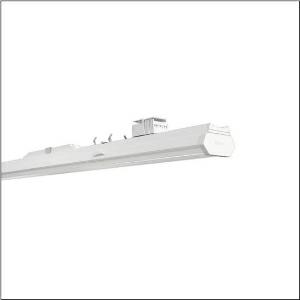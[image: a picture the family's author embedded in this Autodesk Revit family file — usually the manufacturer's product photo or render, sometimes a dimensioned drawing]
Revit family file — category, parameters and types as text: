
# Revit family: licross_21_protected_mo_52td117n485g
name_source: partatom
category: Lighting Fixtures
units: mm (PartAtom-declared; Revit-internal decimal feet)

## family parameters
Cut with Voids When Loaded = No
Host = Face
Light Source = No
Part Type = Normal
Room Calculation Point = No
Round Connector Dimension = Use Diameter
Shared = No

## types (1)
- Licross 21 Protected MO (1 x LED, 8570 lm, 47.9 W, 4000K)
    Apparent Load = 48 VA
    CIE Flux Codes = 83 94 98 100 100
    Color Rendering = 80
    Color Temperature = 4000K
    Default Elevation = 1800 mm
    Description = Licross 21 Protected MO, luminaire insert, of sheet steel, galvanised, coil coated, white, length: 1.500mm, width: 66mm, height: 67mm, LED rated luminous flux: 8.570lm, light colour: 840, SDCM (Standard Deviation of Colour Matching)MacAdam ≤ 3 SDCM (initial), control gear: ON/OFF, with plug, 3-pole, with phase selection, mains connection: 220..240V, AC, 50/60Hz, rated input power: 48W, internal wiring halogen-free, primary light control with lens, of plastic, primary optical cover: cover, of PMMA, light emission: direct distribution, primary light characteristic: symmetric, protection rating (complete): IP54, insulation class (complete): insulation class I (protective earthing), certification: CE, ENEC, VDE, UKCA, protection symbol: D if used in an environment with non-conductive dust loads with corresponding accessories, impact resistance: IK06, permissible ambient temperature for indoor applications: -35..+45°C, corresponds to IFS (International Featured Standards) requirements for safety and quality in the food industry, reducing of maximum allowable ambient temperature of 5°C with ceiling mounting, LABS conformity tested according to VDMA 24364:2018-05, The light source and the operating device comply with the requirements of the Ecodesign Regulation (EU) 2019/2020 and are replaceable in accordance with this regulation, packaging unit: 1 piece
    Height = 92 mm
    Lamp = 1 x LED
    Lamp Light Flux = 8570 lm
    Lamp Power = 47.9 W
    Lamp count = 1
    Length = 1500 mm
    Luminous efficacy = 179 lm/W
    Manufacturer = Siteco
    ModVariant = No
    Model = 52TD117N485G
    Mounting Place = Ceiling
    Mounting Type = Pendant
    Number of Poles = 1
    OnlyDefault = Yes
    Power Factor = 1
    Product Name = Licross 21 Protected MO
    Product group = luminaire insert | ceiling pendant
    ProductGroupID = 901
    Protection Class = Protection class I
    Protection Degree = IP 54
    RLX_Detail_Level = 1
    RLX_Emergency_Light_Flux = 0 lm
    RLX_Emergency_Type = 0
    RLX_Emergency_Type_DB = No
    RlxData = <blob elided: 20681 chars, md5=4c34c8cb>
    Socket = socket
    Standby Power = 0 W
    System Light Flux = 8570 lm
    System Power = 48 W
    Type Comments = Product without accessories
    Type Image = l_1256148.jpg
    URL = http://relux.com
    VarID = ---
    Voltage = 0 V
    Weight = 0.00 kg
    Width = 88 mm

## geometry (parser evidence)
native form markers: Blend x4, Sweep x13
no freeform markers — native parametric forms only
